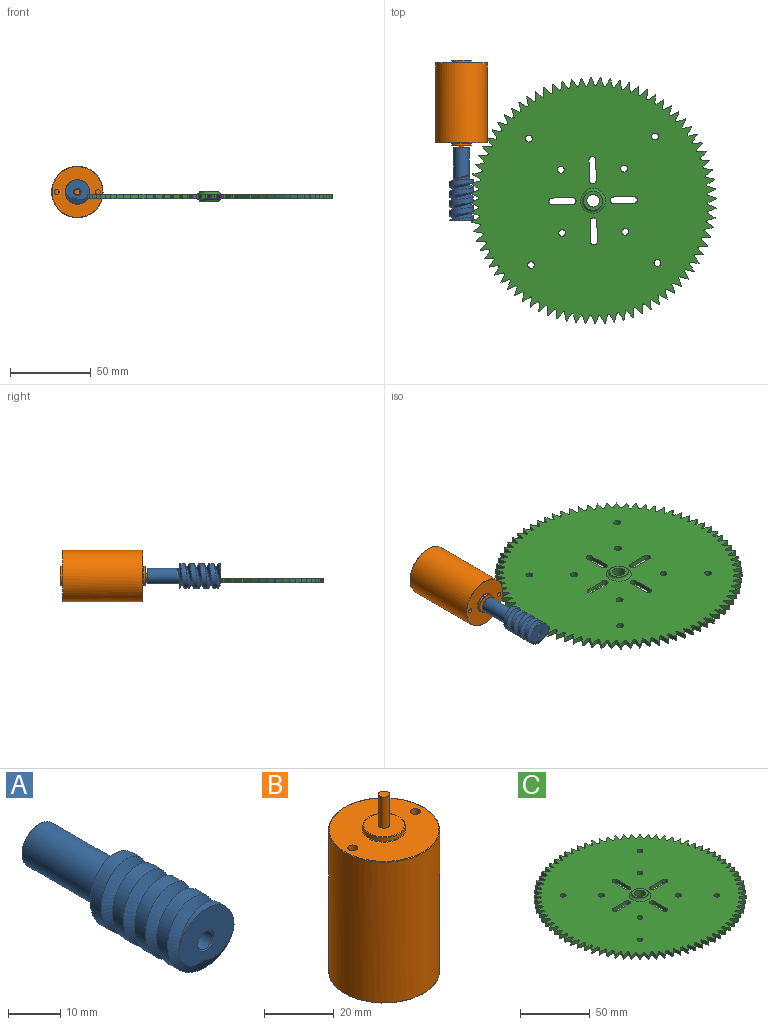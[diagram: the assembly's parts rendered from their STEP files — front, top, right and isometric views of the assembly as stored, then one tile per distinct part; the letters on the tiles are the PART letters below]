
ASSEMBLY  parts=3 mates=1
PART A: 12 faces, bbox 17.3x47.5x15 mm
  f0: cylinder r=4.76mm len=19.75mm, axis (0,-1,0), area 585.3mm2, adj f1,f5,f9,f10,f11
  f1: plane 15x12.23mm, normal (0,1,0), area 73.4mm2, adj f0,f2,f10,f11
  f2: cylinder r=7.5mm len=25.4mm, axis (0,1,0), area 597.9mm2, adj f1,f3,f10,f11
  f3: plane 14.95x12.4mm, normal (0,-1,0), area 127.1mm2, adj f2,f8,f10,f11
  f4: plane 9.03x9.03mm, normal (0,1,0), area 47.2mm2, adj f5,f7
  f5: cone r=4.51mm half-angle=45deg, axis (0,-1,0), area 10.3mm2, adj f0,f4
  f6: cylinder r=2.06mm len=44.9mm, axis (0,1,0), area 582.2mm2, adj f7,f8
  f7: cone r=2.06mm half-angle=45deg, axis (0,1,0), area 4.9mm2, adj f4,f6
  f8: cone r=2.31mm half-angle=45deg, axis (0,-1,0), area 4.9mm2, adj f3,f6
  f9: plane 0.47x0.44mm, normal (-0.5,0,0.87), area 0.1mm2, adj f0,f10,f11
  f10: bspline ~31.5x17.32mm, area 572.4mm2, adj f0,f1,f2,f3,f9,f11
  f11: bspline ~30.5x17.32mm, area 570.9mm2, adj f0,f1,f2,f3,f9,f10
PART B: 21 faces, bbox 34.4x34.4x63.6 mm
  f0: plane 11.63x11.63mm, normal (0,0,1), area 98.6mm2, adj f9,f16
  f1: cylinder r=1.55mm len=26.38mm, axis (0,0,1), area 256.9mm2, adj f2,f8
  f2: plane 11.63x11.63mm, normal (0,0,-1), area 98.7mm2, adj f1,f13
  f3: cylinder r=6.02mm len=12.03mm, axis (0,0,1), area 45.4mm2, adj f12,f13
  f4: plane 31.35x31.35mm, normal (0,0,-1), area 650.6mm2, adj f11,f12
  f5: cylinder r=15.88mm len=49.15mm, axis (0,0,1), area 4902.5mm2, adj f11,f14
  f6: plane 31.35x31.35mm, normal (0,0,1), area 638.2mm2, adj f14,f15,f17,f19
  f7: cylinder r=6.02mm len=12.03mm, axis (0,0,1), area 45.4mm2, adj f15,f16
  f8: plane 3.1x3.1mm, normal (0,0,-1), area 7.5mm2, adj f1
  f9: cylinder r=1.55mm len=10.83mm, axis (0,0,-1), area 105.8mm2, adj f0,f10
  f10: plane 3.11x3.11mm, normal (0,0,1), area 7.6mm2, adj f9
  f11: torus R=15.68mm, axis (0,0,-1), area 31.2mm2, adj f4,f5
  f12: torus R=6.21mm, axis (0,0,-1), area 12mm2, adj f3,f4
  f13: torus R=5.81mm, axis (0,0,-1), area 11.7mm2, adj f2,f3
  f14: torus R=15.68mm, axis (0,0,1), area 31.2mm2, adj f5,f6
  f15: torus R=6.21mm, axis (0,0,1), area 12mm2, adj f6,f7
  f16: torus R=5.81mm, axis (0,0,1), area 11.7mm2, adj f0,f7
  f17: cylinder r=1.4mm len=5mm, axis (0,0,1), area 44mm2, adj f6,f18
  f18: plane 2.8x2.8mm, normal (0,0,1), area 6.2mm2, adj f17
  f19: cylinder r=1.4mm len=5mm, axis (0,0,1), area 44mm2, adj f6,f20
  f20: plane 2.8x2.8mm, normal (0,0,1), area 6.2mm2, adj f19
PART C: 351 faces, bbox 152.4x152.4x9.2 mm
  f0: plane 152.4x152.4mm, normal (0,0,-1), area 16289.8mm2, adj f1,f2,f3,f4,f5,f6,f7,f8
  f1: cylinder r=76.2mm len=2.92mm, axis (0,0,-1), area 0.8mm2, adj f0,f81,f84,f320
  f2: cylinder r=76.2mm len=2.92mm, axis (0,0,-1), area 0.8mm2, adj f0,f81,f317,f321
  f3: cylinder r=76.2mm len=2.92mm, axis (0,0,-1), area 0.8mm2, adj f0,f81,f314,f318
  f4: cylinder r=76.2mm len=2.92mm, axis (0,0,-1), area 0.8mm2, adj f0,f81,f311,f315
  f5: cylinder r=76.2mm len=2.92mm, axis (0,0,-1), area 0.8mm2, adj f0,f81,f308,f312
  f6: cylinder r=76.2mm len=2.92mm, axis (0,0,-1), area 0.8mm2, adj f0,f81,f305,f309
  f7: cylinder r=76.2mm len=2.92mm, axis (0,0,-1), area 0.8mm2, adj f0,f81,f302,f306
  f8: cylinder r=76.2mm len=2.92mm, axis (0,0,-1), area 0.8mm2, adj f0,f81,f299,f303
  f9: cylinder r=76.2mm len=2.92mm, axis (0,0,-1), area 0.8mm2, adj f0,f81,f296,f300
  f10: cylinder r=76.2mm len=2.92mm, axis (0,0,-1), area 0.8mm2, adj f0,f81,f293,f297
  f11: cylinder r=76.2mm len=2.92mm, axis (0,0,-1), area 0.8mm2, adj f0,f81,f290,f294
  f12: cylinder r=76.2mm len=2.92mm, axis (0,0,-1), area 0.8mm2, adj f0,f81,f287,f291
  f13: cylinder r=76.2mm len=2.92mm, axis (0,0,-1), area 0.8mm2, adj f0,f81,f284,f288
  f14: cylinder r=76.2mm len=2.92mm, axis (0,0,-1), area 0.8mm2, adj f0,f81,f281,f285
  f15: cylinder r=76.2mm len=2.92mm, axis (0,0,-1), area 0.8mm2, adj f0,f81,f278,f282
  f16: cylinder r=76.2mm len=2.92mm, axis (0,0,-1), area 0.8mm2, adj f0,f81,f275,f279
  f17: cylinder r=76.2mm len=2.92mm, axis (0,0,-1), area 0.8mm2, adj f0,f81,f272,f276
  f18: cylinder r=76.2mm len=2.92mm, axis (0,0,-1), area 0.8mm2, adj f0,f81,f269,f273
  f19: cylinder r=76.2mm len=2.92mm, axis (0,0,-1), area 0.8mm2, adj f0,f81,f266,f270
  f20: cylinder r=76.2mm len=2.92mm, axis (0,0,-1), area 0.8mm2, adj f0,f81,f263,f267
  f21: cylinder r=76.2mm len=2.92mm, axis (0,0,-1), area 0.8mm2, adj f0,f81,f260,f264
  f22: cylinder r=76.2mm len=2.92mm, axis (0,0,-1), area 0.8mm2, adj f0,f81,f257,f261
  f23: cylinder r=76.2mm len=2.92mm, axis (0,0,-1), area 0.8mm2, adj f0,f81,f254,f258
  f24: cylinder r=76.2mm len=2.92mm, axis (0,0,-1), area 0.8mm2, adj f0,f81,f251,f255
  f25: cylinder r=76.2mm len=2.92mm, axis (0,0,-1), area 0.8mm2, adj f0,f81,f248,f252
  f26: cylinder r=76.2mm len=2.92mm, axis (0,0,-1), area 0.8mm2, adj f0,f81,f245,f249
  f27: cylinder r=76.2mm len=2.92mm, axis (0,0,-1), area 0.8mm2, adj f0,f81,f242,f246
  f28: cylinder r=76.2mm len=2.92mm, axis (0,0,-1), area 0.8mm2, adj f0,f81,f239,f243
  f29: cylinder r=76.2mm len=2.92mm, axis (0,0,-1), area 0.8mm2, adj f0,f81,f236,f240
  f30: cylinder r=76.2mm len=2.92mm, axis (0,0,-1), area 0.8mm2, adj f0,f81,f233,f237
  f31: cylinder r=76.2mm len=2.92mm, axis (0,0,-1), area 0.8mm2, adj f0,f81,f230,f234
  f32: cylinder r=76.2mm len=2.92mm, axis (0,0,-1), area 0.8mm2, adj f0,f81,f227,f231
  f33: cylinder r=76.2mm len=2.92mm, axis (0,0,-1), area 0.8mm2, adj f0,f81,f224,f228
  f34: cylinder r=76.2mm len=2.92mm, axis (0,0,-1), area 0.8mm2, adj f0,f81,f221,f225
  f35: cylinder r=76.2mm len=2.92mm, axis (0,0,-1), area 0.8mm2, adj f0,f81,f218,f222
  f36: cylinder r=76.2mm len=2.92mm, axis (0,0,-1), area 0.8mm2, adj f0,f81,f215,f219
  f37: cylinder r=76.2mm len=2.92mm, axis (0,0,-1), area 0.8mm2, adj f0,f81,f212,f216
  f38: cylinder r=76.2mm len=2.92mm, axis (0,0,-1), area 0.8mm2, adj f0,f81,f209,f213
  f39: cylinder r=76.2mm len=2.92mm, axis (0,0,-1), area 0.8mm2, adj f0,f81,f206,f210
  f40: cylinder r=76.2mm len=2.92mm, axis (0,0,-1), area 0.8mm2, adj f0,f81,f203,f207
  f41: cylinder r=76.2mm len=2.92mm, axis (0,0,-1), area 0.8mm2, adj f0,f81,f200,f204
  f42: cylinder r=76.2mm len=2.92mm, axis (0,0,-1), area 0.8mm2, adj f0,f81,f197,f201
  f43: cylinder r=76.2mm len=2.92mm, axis (0,0,-1), area 0.8mm2, adj f0,f81,f194,f198
  f44: cylinder r=76.2mm len=2.92mm, axis (0,0,-1), area 0.8mm2, adj f0,f81,f191,f195
  f45: cylinder r=76.2mm len=2.92mm, axis (0,0,-1), area 0.8mm2, adj f0,f81,f188,f192
  f46: cylinder r=76.2mm len=2.92mm, axis (0,0,-1), area 0.8mm2, adj f0,f81,f185,f189
  f47: cylinder r=76.2mm len=2.92mm, axis (0,0,-1), area 0.8mm2, adj f0,f81,f182,f186
  f48: cylinder r=76.2mm len=2.92mm, axis (0,0,-1), area 0.8mm2, adj f0,f81,f179,f183
  f49: cylinder r=76.2mm len=2.92mm, axis (0,0,-1), area 0.8mm2, adj f0,f81,f176,f180
  f50: cylinder r=76.2mm len=2.92mm, axis (0,0,-1), area 0.8mm2, adj f0,f81,f173,f177
  f51: cylinder r=76.2mm len=2.92mm, axis (0,0,-1), area 0.8mm2, adj f0,f81,f170,f174
  f52: cylinder r=76.2mm len=2.92mm, axis (0,0,-1), area 0.8mm2, adj f0,f81,f167,f171
  f53: cylinder r=76.2mm len=2.92mm, axis (0,0,-1), area 0.8mm2, adj f0,f81,f164,f168
  f54: cylinder r=76.2mm len=2.92mm, axis (0,0,-1), area 0.8mm2, adj f0,f81,f161,f165
  f55: cylinder r=76.2mm len=2.92mm, axis (0,0,-1), area 0.8mm2, adj f0,f81,f158,f162
  f56: cylinder r=76.2mm len=2.92mm, axis (0,0,-1), area 0.8mm2, adj f0,f81,f155,f159
  f57: cylinder r=76.2mm len=2.92mm, axis (0,0,-1), area 0.8mm2, adj f0,f81,f152,f156
  f58: cylinder r=76.2mm len=2.92mm, axis (0,0,-1), area 0.8mm2, adj f0,f81,f149,f153
  f59: cylinder r=76.2mm len=2.92mm, axis (0,0,-1), area 0.8mm2, adj f0,f81,f146,f150
  f60: cylinder r=76.2mm len=2.92mm, axis (0,0,-1), area 0.8mm2, adj f0,f81,f143,f147
  f61: cylinder r=76.2mm len=2.92mm, axis (0,0,-1), area 0.8mm2, adj f0,f81,f140,f144
  f62: cylinder r=76.2mm len=2.92mm, axis (0,0,-1), area 0.8mm2, adj f0,f81,f137,f141
  f63: cylinder r=76.2mm len=2.92mm, axis (0,0,-1), area 0.8mm2, adj f0,f81,f134,f138
  f64: cylinder r=76.2mm len=2.92mm, axis (0,0,-1), area 0.8mm2, adj f0,f81,f131,f135
  f65: cylinder r=76.2mm len=2.92mm, axis (0,0,-1), area 0.8mm2, adj f0,f81,f128,f132
  f66: cylinder r=76.2mm len=2.92mm, axis (0,0,-1), area 0.8mm2, adj f0,f81,f125,f129
  f67: cylinder r=76.2mm len=2.92mm, axis (0,0,-1), area 0.8mm2, adj f0,f81,f122,f126
  f68: cylinder r=76.2mm len=2.92mm, axis (0,0,-1), area 0.8mm2, adj f0,f81,f119,f123
  f69: cylinder r=76.2mm len=2.92mm, axis (0,0,-1), area 0.8mm2, adj f0,f81,f116,f120
  f70: cylinder r=76.2mm len=2.92mm, axis (0,0,-1), area 0.8mm2, adj f0,f81,f113,f117
  f71: cylinder r=76.2mm len=2.92mm, axis (0,0,-1), area 0.8mm2, adj f0,f81,f110,f114
  f72: cylinder r=76.2mm len=2.92mm, axis (0,0,-1), area 0.8mm2, adj f0,f81,f107,f111
  f73: cylinder r=76.2mm len=2.92mm, axis (0,0,-1), area 0.8mm2, adj f0,f81,f104,f108
  f74: cylinder r=76.2mm len=2.92mm, axis (0,0,-1), area 0.8mm2, adj f0,f81,f101,f105
  f75: cylinder r=76.2mm len=2.92mm, axis (0,0,-1), area 0.8mm2, adj f0,f81,f98,f102
  f76: cylinder r=76.2mm len=2.92mm, axis (0,0,-1), area 0.8mm2, adj f0,f81,f95,f99
  f77: cylinder r=76.2mm len=2.92mm, axis (0,0,-1), area 0.8mm2, adj f0,f81,f92,f96
  f78: cylinder r=76.2mm len=2.92mm, axis (0,0,-1), area 0.8mm2, adj f0,f81,f89,f93
  f79: cylinder r=76.2mm len=2.92mm, axis (0,0,-1), area 0.8mm2, adj f0,f81,f86,f90
  f80: cylinder r=76.2mm len=2.92mm, axis (0,0,-1), area 0.8mm2, adj f0,f81,f83,f87
  f81: plane 152.4x152.4mm, normal (0,0,1), area 16289.8mm2, adj f1,f2,f3,f4,f5,f6,f7,f8
  f82: cylinder r=71.06mm len=2.92mm, axis (0,0,-1), area 2.9mm2, adj f0,f81,f83,f84
  f83: plane 5x2.92mm, normal (0.89,-0.45,0), area 16.4mm2, adj f0,f80,f81,f82
  f84: plane 5.18x2.92mm, normal (-0.92,-0.38,0), area 16.4mm2, adj f0,f1,f81,f82
  f85: cylinder r=71.06mm len=2.92mm, axis (0,0,-1), area 2.9mm2, adj f0,f81,f86,f87
  f86: plane 4.78x2.93mm, normal (0.85,-0.52,0), area 16.4mm2, adj f0,f79,f81,f85
  f87: plane 5.33x2.92mm, normal (-0.95,-0.31,0), area 16.4mm2, adj f0,f80,f81,f85
  f88: cylinder r=71.06mm len=2.92mm, axis (0,0,-1), area 2.9mm2, adj f0,f81,f89,f90
  f89: plane 4.54x3.3mm, normal (0.81,-0.59,0), area 16.4mm2, adj f0,f78,f81,f88
  f90: plane 5.45x2.92mm, normal (-0.97,-0.23,0), area 16.4mm2, adj f0,f79,f81,f88
  f91: cylinder r=71.06mm len=2.92mm, axis (0,0,-1), area 2.9mm2, adj f0,f81,f92,f93
  f92: plane 4.26x3.64mm, normal (0.76,-0.65,0), area 16.4mm2, adj f0,f77,f81,f91
  f93: plane 5.54x2.92mm, normal (-0.99,-0.16,0), area 16.4mm2, adj f0,f78,f81,f91
  f94: cylinder r=71.06mm len=2.92mm, axis (0,0,-1), area 2.9mm2, adj f0,f81,f95,f96
  f95: plane 3.97x3.97mm, normal (0.71,-0.71,0), area 16.4mm2, adj f0,f76,f81,f94
  f96: plane 5.59x2.92mm, normal (-1,-0.08,0), area 16.4mm2, adj f0,f77,f81,f94
  f97: cylinder r=71.06mm len=2.92mm, axis (0,0,-1), area 2.9mm2, adj f0,f81,f98,f99
  f98: plane 4.27x3.64mm, normal (0.65,-0.76,0), area 16.4mm2, adj f0,f75,f81,f97
  f99: plane 5.61x2.92mm, normal (-1,0,0), area 16.4mm2, adj f0,f76,f81,f97
  f100: cylinder r=71.06mm len=2.92mm, axis (0,0,-1), area 2.9mm2, adj f0,f81,f101,f102
  f101: plane 4.54x3.3mm, normal (0.59,-0.81,0), area 16.4mm2, adj f0,f74,f81,f100
  f102: plane 5.59x2.92mm, normal (-1,0.08,0), area 16.4mm2, adj f0,f75,f81,f100
  f103: cylinder r=71.06mm len=2.92mm, axis (0,0,-1), area 2.9mm2, adj f0,f81,f104,f105
  f104: plane 4.78x2.93mm, normal (0.52,-0.85,0), area 16.4mm2, adj f0,f73,f81,f103
  f105: plane 5.54x2.92mm, normal (-0.99,0.16,0), area 16.4mm2, adj f0,f74,f81,f103
  f106: cylinder r=71.06mm len=2.92mm, axis (0,0,-1), area 2.9mm2, adj f0,f81,f107,f108
  f107: plane 5x2.92mm, normal (0.45,-0.89,0), area 16.4mm2, adj f0,f72,f81,f106
  f108: plane 5.45x2.92mm, normal (-0.97,0.23,0), area 16.4mm2, adj f0,f73,f81,f106
  f109: cylinder r=71.06mm len=2.92mm, axis (0,0,-1), area 2.9mm2, adj f0,f81,f110,f111
  f110: plane 5.18x2.92mm, normal (0.38,-0.92,0), area 16.4mm2, adj f0,f71,f81,f109
  f111: plane 5.33x2.92mm, normal (-0.95,0.31,0), area 16.4mm2, adj f0,f72,f81,f109
  f112: cylinder r=71.06mm len=2.92mm, axis (0,0,-1), area 2.9mm2, adj f0,f81,f113,f114
  f113: plane 5.34x2.92mm, normal (0.31,-0.95,0), area 16.4mm2, adj f0,f70,f81,f112
  f114: plane 5.18x2.92mm, normal (-0.92,0.38,0), area 16.4mm2, adj f0,f71,f81,f112
  f115: cylinder r=71.06mm len=2.92mm, axis (0,0,-1), area 2.9mm2, adj f0,f81,f116,f117
  f116: plane 5.45x2.92mm, normal (0.23,-0.97,0), area 16.4mm2, adj f0,f69,f81,f115
  f117: plane 5x2.92mm, normal (-0.89,0.45,0), area 16.4mm2, adj f0,f70,f81,f115
  f118: cylinder r=71.06mm len=2.92mm, axis (0,0,-1), area 2.9mm2, adj f0,f81,f119,f120
  f119: plane 5.54x2.92mm, normal (0.16,-0.99,0), area 16.4mm2, adj f0,f68,f81,f118
  f120: plane 4.78x2.93mm, normal (-0.85,0.52,0), area 16.4mm2, adj f0,f69,f81,f118
  f121: cylinder r=71.06mm len=2.92mm, axis (0,0,-1), area 2.9mm2, adj f0,f81,f122,f123
  f122: plane 5.59x2.92mm, normal (0.08,-1,0), area 16.4mm2, adj f0,f67,f81,f121
  f123: plane 4.54x3.3mm, normal (-0.81,0.59,0), area 16.4mm2, adj f0,f68,f81,f121
  f124: cylinder r=71.06mm len=2.92mm, axis (0,0,-1), area 2.9mm2, adj f0,f81,f125,f126
  f125: plane 5.61x2.92mm, normal (0,-1,0), area 16.4mm2, adj f0,f66,f81,f124
  f126: plane 4.27x3.64mm, normal (-0.76,0.65,0), area 16.4mm2, adj f0,f67,f81,f124
  f127: cylinder r=71.06mm len=2.92mm, axis (0,0,-1), area 2.9mm2, adj f0,f81,f128,f129
  f128: plane 5.59x2.92mm, normal (-0.08,-1,0), area 16.4mm2, adj f0,f65,f81,f127
  f129: plane 3.97x3.97mm, normal (-0.71,0.71,0), area 16.4mm2, adj f0,f66,f81,f127
  f130: cylinder r=71.06mm len=2.92mm, axis (0,0,-1), area 2.9mm2, adj f0,f81,f131,f132
  f131: plane 5.54x2.92mm, normal (-0.16,-0.99,0), area 16.4mm2, adj f0,f64,f81,f130
  f132: plane 4.27x3.64mm, normal (-0.65,0.76,0), area 16.4mm2, adj f0,f65,f81,f130
  f133: cylinder r=71.06mm len=2.92mm, axis (0,0,-1), area 2.9mm2, adj f0,f81,f134,f135
  f134: plane 5.45x2.92mm, normal (-0.23,-0.97,0), area 16.4mm2, adj f0,f63,f81,f133
  f135: plane 4.54x3.3mm, normal (-0.59,0.81,0), area 16.4mm2, adj f0,f64,f81,f133
  f136: cylinder r=71.06mm len=2.92mm, axis (0,0,-1), area 2.9mm2, adj f0,f81,f137,f138
  f137: plane 5.33x2.92mm, normal (-0.31,-0.95,0), area 16.4mm2, adj f0,f62,f81,f136
  f138: plane 4.78x2.93mm, normal (-0.52,0.85,0), area 16.4mm2, adj f0,f63,f81,f136
  f139: cylinder r=71.06mm len=2.92mm, axis (0,0,-1), area 2.9mm2, adj f0,f81,f140,f141
  f140: plane 5.18x2.92mm, normal (-0.38,-0.92,0), area 16.4mm2, adj f0,f61,f81,f139
  f141: plane 5x2.92mm, normal (-0.45,0.89,0), area 16.4mm2, adj f0,f62,f81,f139
  f142: cylinder r=71.06mm len=2.92mm, axis (0,0,-1), area 2.9mm2, adj f0,f81,f143,f144
  f143: plane 5x2.92mm, normal (-0.45,-0.89,0), area 16.4mm2, adj f0,f60,f81,f142
  f144: plane 5.18x2.92mm, normal (-0.38,0.92,0), area 16.4mm2, adj f0,f61,f81,f142
  f145: cylinder r=71.06mm len=2.92mm, axis (0,0,-1), area 2.9mm2, adj f0,f81,f146,f147
  f146: plane 4.78x2.93mm, normal (-0.52,-0.85,0), area 16.4mm2, adj f0,f59,f81,f145
  f147: plane 5.33x2.92mm, normal (-0.31,0.95,0), area 16.4mm2, adj f0,f60,f81,f145
  f148: cylinder r=71.06mm len=2.92mm, axis (0,0,-1), area 2.9mm2, adj f0,f81,f149,f150
  f149: plane 4.54x3.3mm, normal (-0.59,-0.81,0), area 16.4mm2, adj f0,f58,f81,f148
  f150: plane 5.45x2.92mm, normal (-0.23,0.97,0), area 16.4mm2, adj f0,f59,f81,f148
  f151: cylinder r=71.06mm len=2.92mm, axis (0,0,-1), area 2.9mm2, adj f0,f81,f152,f153
  f152: plane 4.26x3.64mm, normal (-0.65,-0.76,0), area 16.4mm2, adj f0,f57,f81,f151
  f153: plane 5.54x2.92mm, normal (-0.16,0.99,0), area 16.4mm2, adj f0,f58,f81,f151
  f154: cylinder r=71.06mm len=2.92mm, axis (0,0,-1), area 2.9mm2, adj f0,f81,f155,f156
  f155: plane 3.97x3.97mm, normal (-0.71,-0.71,0), area 16.4mm2, adj f0,f56,f81,f154
  f156: plane 5.59x2.92mm, normal (-0.08,1,0), area 16.4mm2, adj f0,f57,f81,f154
  f157: cylinder r=71.06mm len=2.92mm, axis (0,0,-1), area 2.9mm2, adj f0,f81,f158,f159
  f158: plane 4.27x3.64mm, normal (-0.76,-0.65,0), area 16.4mm2, adj f0,f55,f81,f157
  f159: plane 5.61x2.92mm, normal (0,1,0), area 16.4mm2, adj f0,f56,f81,f157
  f160: cylinder r=71.06mm len=2.92mm, axis (0,0,-1), area 2.9mm2, adj f0,f81,f161,f162
  f161: plane 4.54x3.3mm, normal (-0.81,-0.59,0), area 16.4mm2, adj f0,f54,f81,f160
  f162: plane 5.59x2.92mm, normal (0.08,1,0), area 16.4mm2, adj f0,f55,f81,f160
  f163: cylinder r=71.06mm len=2.92mm, axis (0,0,-1), area 2.9mm2, adj f0,f81,f164,f165
  f164: plane 4.78x2.93mm, normal (-0.85,-0.52,0), area 16.4mm2, adj f0,f53,f81,f163
  f165: plane 5.54x2.92mm, normal (0.16,0.99,0), area 16.4mm2, adj f0,f54,f81,f163
  f166: cylinder r=71.06mm len=2.92mm, axis (0,0,-1), area 2.9mm2, adj f0,f81,f167,f168
  f167: plane 5x2.92mm, normal (-0.89,-0.45,0), area 16.4mm2, adj f0,f52,f81,f166
  f168: plane 5.45x2.92mm, normal (0.23,0.97,0), area 16.4mm2, adj f0,f53,f81,f166
  f169: cylinder r=71.06mm len=2.92mm, axis (0,0,-1), area 2.9mm2, adj f0,f81,f170,f171
  f170: plane 5.18x2.92mm, normal (-0.92,-0.38,0), area 16.4mm2, adj f0,f51,f81,f169
  f171: plane 5.33x2.92mm, normal (0.31,0.95,0), area 16.4mm2, adj f0,f52,f81,f169
  f172: cylinder r=71.06mm len=2.92mm, axis (0,0,-1), area 2.9mm2, adj f0,f81,f173,f174
  f173: plane 5.34x2.92mm, normal (-0.95,-0.31,0), area 16.4mm2, adj f0,f50,f81,f172
  f174: plane 5.18x2.92mm, normal (0.38,0.92,0), area 16.4mm2, adj f0,f51,f81,f172
  f175: cylinder r=71.06mm len=2.92mm, axis (0,0,-1), area 2.9mm2, adj f0,f81,f176,f177
  f176: plane 5.45x2.92mm, normal (-0.97,-0.23,0), area 16.4mm2, adj f0,f49,f81,f175
  f177: plane 5x2.92mm, normal (0.45,0.89,0), area 16.4mm2, adj f0,f50,f81,f175
  f178: cylinder r=71.06mm len=2.92mm, axis (0,0,-1), area 2.9mm2, adj f0,f81,f179,f180
  f179: plane 5.54x2.92mm, normal (-0.99,-0.16,0), area 16.4mm2, adj f0,f48,f81,f178
  f180: plane 4.78x2.93mm, normal (0.52,0.85,0), area 16.4mm2, adj f0,f49,f81,f178
  f181: cylinder r=71.06mm len=2.92mm, axis (0,0,-1), area 2.9mm2, adj f0,f81,f182,f183
  f182: plane 5.59x2.92mm, normal (-1,-0.08,0), area 16.4mm2, adj f0,f47,f81,f181
  f183: plane 4.54x3.3mm, normal (0.59,0.81,0), area 16.4mm2, adj f0,f48,f81,f181
  f184: cylinder r=71.06mm len=2.92mm, axis (0,0,-1), area 2.9mm2, adj f0,f81,f185,f186
  f185: plane 5.61x2.92mm, normal (-1,0,0), area 16.4mm2, adj f0,f46,f81,f184
  f186: plane 4.27x3.64mm, normal (0.65,0.76,0), area 16.4mm2, adj f0,f47,f81,f184
  f187: cylinder r=71.06mm len=2.92mm, axis (0,0,-1), area 2.9mm2, adj f0,f81,f188,f189
  f188: plane 5.59x2.92mm, normal (-1,0.08,0), area 16.4mm2, adj f0,f45,f81,f187
  f189: plane 3.97x3.97mm, normal (0.71,0.71,0), area 16.4mm2, adj f0,f46,f81,f187
  f190: cylinder r=71.06mm len=2.92mm, axis (0,0,-1), area 2.9mm2, adj f0,f81,f191,f192
  f191: plane 5.54x2.92mm, normal (-0.99,0.16,0), area 16.4mm2, adj f0,f44,f81,f190
  f192: plane 4.27x3.64mm, normal (0.76,0.65,0), area 16.4mm2, adj f0,f45,f81,f190
  f193: cylinder r=71.06mm len=2.92mm, axis (0,0,-1), area 2.9mm2, adj f0,f81,f194,f195
  f194: plane 5.45x2.92mm, normal (-0.97,0.23,0), area 16.4mm2, adj f0,f43,f81,f193
  f195: plane 4.54x3.3mm, normal (0.81,0.59,0), area 16.4mm2, adj f0,f44,f81,f193
  f196: cylinder r=71.06mm len=2.92mm, axis (0,0,-1), area 2.9mm2, adj f0,f81,f197,f198
  f197: plane 5.33x2.92mm, normal (-0.95,0.31,0), area 16.4mm2, adj f0,f42,f81,f196
  f198: plane 4.78x2.93mm, normal (0.85,0.52,0), area 16.4mm2, adj f0,f43,f81,f196
  f199: cylinder r=71.06mm len=2.92mm, axis (0,0,-1), area 2.9mm2, adj f0,f81,f200,f201
  f200: plane 5.18x2.92mm, normal (-0.92,0.38,0), area 16.4mm2, adj f0,f41,f81,f199
  f201: plane 5x2.92mm, normal (0.89,0.45,0), area 16.4mm2, adj f0,f42,f81,f199
  f202: cylinder r=71.06mm len=2.92mm, axis (0,0,-1), area 2.9mm2, adj f0,f81,f203,f204
  f203: plane 5x2.92mm, normal (-0.89,0.45,0), area 16.4mm2, adj f0,f40,f81,f202
  f204: plane 5.18x2.92mm, normal (0.92,0.38,0), area 16.4mm2, adj f0,f41,f81,f202
  f205: cylinder r=71.06mm len=2.92mm, axis (0,0,-1), area 2.9mm2, adj f0,f81,f206,f207
  f206: plane 4.78x2.93mm, normal (-0.85,0.52,0), area 16.4mm2, adj f0,f39,f81,f205
  f207: plane 5.33x2.92mm, normal (0.95,0.31,0), area 16.4mm2, adj f0,f40,f81,f205
  f208: cylinder r=71.06mm len=2.92mm, axis (0,0,-1), area 2.9mm2, adj f0,f81,f209,f210
  f209: plane 4.54x3.3mm, normal (-0.81,0.59,0), area 16.4mm2, adj f0,f38,f81,f208
  f210: plane 5.45x2.92mm, normal (0.97,0.23,0), area 16.4mm2, adj f0,f39,f81,f208
  f211: cylinder r=71.06mm len=2.92mm, axis (0,0,-1), area 2.9mm2, adj f0,f81,f212,f213
  f212: plane 4.26x3.64mm, normal (-0.76,0.65,0), area 16.4mm2, adj f0,f37,f81,f211
  f213: plane 5.54x2.92mm, normal (0.99,0.16,0), area 16.4mm2, adj f0,f38,f81,f211
  f214: cylinder r=71.06mm len=2.92mm, axis (0,0,-1), area 2.9mm2, adj f0,f81,f215,f216
  f215: plane 3.97x3.97mm, normal (-0.71,0.71,0), area 16.4mm2, adj f0,f36,f81,f214
  f216: plane 5.59x2.92mm, normal (1,0.08,0), area 16.4mm2, adj f0,f37,f81,f214
  f217: cylinder r=71.06mm len=2.92mm, axis (0,0,-1), area 2.9mm2, adj f0,f81,f218,f219
  f218: plane 4.27x3.64mm, normal (-0.65,0.76,0), area 16.4mm2, adj f0,f35,f81,f217
  f219: plane 5.61x2.92mm, normal (1,0,0), area 16.4mm2, adj f0,f36,f81,f217
  f220: cylinder r=71.06mm len=2.92mm, axis (0,0,-1), area 2.9mm2, adj f0,f81,f221,f222
  f221: plane 4.54x3.3mm, normal (-0.59,0.81,0), area 16.4mm2, adj f0,f34,f81,f220
  f222: plane 5.59x2.92mm, normal (1,-0.08,0), area 16.4mm2, adj f0,f35,f81,f220
  f223: cylinder r=71.06mm len=2.92mm, axis (0,0,-1), area 2.9mm2, adj f0,f81,f224,f225
  f224: plane 4.78x2.93mm, normal (-0.52,0.85,0), area 16.4mm2, adj f0,f33,f81,f223
  f225: plane 5.54x2.92mm, normal (0.99,-0.16,0), area 16.4mm2, adj f0,f34,f81,f223
  f226: cylinder r=71.06mm len=2.92mm, axis (0,0,-1), area 2.9mm2, adj f0,f81,f227,f228
  f227: plane 5x2.92mm, normal (-0.45,0.89,0), area 16.4mm2, adj f0,f32,f81,f226
  f228: plane 5.45x2.92mm, normal (0.97,-0.23,0), area 16.4mm2, adj f0,f33,f81,f226
  f229: cylinder r=71.06mm len=2.92mm, axis (0,0,-1), area 2.9mm2, adj f0,f81,f230,f231
  f230: plane 5.18x2.92mm, normal (-0.38,0.92,0), area 16.4mm2, adj f0,f31,f81,f229
  f231: plane 5.33x2.92mm, normal (0.95,-0.31,0), area 16.4mm2, adj f0,f32,f81,f229
  f232: cylinder r=71.06mm len=2.92mm, axis (0,0,-1), area 2.9mm2, adj f0,f81,f233,f234
  f233: plane 5.34x2.92mm, normal (-0.31,0.95,0), area 16.4mm2, adj f0,f30,f81,f232
  f234: plane 5.18x2.92mm, normal (0.92,-0.38,0), area 16.4mm2, adj f0,f31,f81,f232
  f235: cylinder r=71.06mm len=2.92mm, axis (0,0,-1), area 2.9mm2, adj f0,f81,f236,f237
  f236: plane 5.45x2.92mm, normal (-0.23,0.97,0), area 16.4mm2, adj f0,f29,f81,f235
  f237: plane 5x2.92mm, normal (0.89,-0.45,0), area 16.4mm2, adj f0,f30,f81,f235
  f238: cylinder r=71.06mm len=2.92mm, axis (0,0,-1), area 2.9mm2, adj f0,f81,f239,f240
  f239: plane 5.54x2.92mm, normal (-0.16,0.99,0), area 16.4mm2, adj f0,f28,f81,f238
  f240: plane 4.78x2.93mm, normal (0.85,-0.52,0), area 16.4mm2, adj f0,f29,f81,f238
  f241: cylinder r=71.06mm len=2.92mm, axis (0,0,-1), area 2.9mm2, adj f0,f81,f242,f243
  f242: plane 5.59x2.92mm, normal (-0.08,1,0), area 16.4mm2, adj f0,f27,f81,f241
  f243: plane 4.54x3.3mm, normal (0.81,-0.59,0), area 16.4mm2, adj f0,f28,f81,f241
  f244: cylinder r=71.06mm len=2.92mm, axis (0,0,-1), area 2.9mm2, adj f0,f81,f245,f246
  f245: plane 5.61x2.92mm, normal (0,1,0), area 16.4mm2, adj f0,f26,f81,f244
  f246: plane 4.27x3.64mm, normal (0.76,-0.65,0), area 16.4mm2, adj f0,f27,f81,f244
  f247: cylinder r=71.06mm len=2.92mm, axis (0,0,-1), area 2.9mm2, adj f0,f81,f248,f249
  f248: plane 5.59x2.92mm, normal (0.08,1,0), area 16.4mm2, adj f0,f25,f81,f247
  f249: plane 3.97x3.97mm, normal (0.71,-0.71,0), area 16.4mm2, adj f0,f26,f81,f247
  f250: cylinder r=71.06mm len=2.92mm, axis (0,0,-1), area 2.9mm2, adj f0,f81,f251,f252
  f251: plane 5.54x2.92mm, normal (0.16,0.99,0), area 16.4mm2, adj f0,f24,f81,f250
  f252: plane 4.27x3.64mm, normal (0.65,-0.76,0), area 16.4mm2, adj f0,f25,f81,f250
  f253: cylinder r=71.06mm len=2.92mm, axis (0,0,-1), area 2.9mm2, adj f0,f81,f254,f255
  f254: plane 5.45x2.92mm, normal (0.23,0.97,0), area 16.4mm2, adj f0,f23,f81,f253
  f255: plane 4.54x3.3mm, normal (0.59,-0.81,0), area 16.4mm2, adj f0,f24,f81,f253
  f256: cylinder r=71.06mm len=2.92mm, axis (0,0,-1), area 2.9mm2, adj f0,f81,f257,f258
  f257: plane 5.33x2.92mm, normal (0.31,0.95,0), area 16.4mm2, adj f0,f22,f81,f256
  f258: plane 4.78x2.93mm, normal (0.52,-0.85,0), area 16.4mm2, adj f0,f23,f81,f256
  f259: cylinder r=71.06mm len=2.92mm, axis (0,0,-1), area 2.9mm2, adj f0,f81,f260,f261
  f260: plane 5.18x2.92mm, normal (0.38,0.92,0), area 16.4mm2, adj f0,f21,f81,f259
  f261: plane 5x2.92mm, normal (0.45,-0.89,0), area 16.4mm2, adj f0,f22,f81,f259
  f262: cylinder r=71.06mm len=2.92mm, axis (0,0,-1), area 2.9mm2, adj f0,f81,f263,f264
  f263: plane 5x2.92mm, normal (0.45,0.89,0), area 16.4mm2, adj f0,f20,f81,f262
  f264: plane 5.18x2.92mm, normal (0.38,-0.92,0), area 16.4mm2, adj f0,f21,f81,f262
  f265: cylinder r=71.06mm len=2.92mm, axis (0,0,-1), area 2.9mm2, adj f0,f81,f266,f267
  f266: plane 4.78x2.93mm, normal (0.52,0.85,0), area 16.4mm2, adj f0,f19,f81,f265
  f267: plane 5.33x2.92mm, normal (0.31,-0.95,0), area 16.4mm2, adj f0,f20,f81,f265
  f268: cylinder r=71.06mm len=2.92mm, axis (0,0,-1), area 2.9mm2, adj f0,f81,f269,f270
  f269: plane 4.54x3.3mm, normal (0.59,0.81,0), area 16.4mm2, adj f0,f18,f81,f268
  f270: plane 5.45x2.92mm, normal (0.23,-0.97,0), area 16.4mm2, adj f0,f19,f81,f268
  f271: cylinder r=71.06mm len=2.92mm, axis (0,0,-1), area 2.9mm2, adj f0,f81,f272,f273
  f272: plane 4.26x3.64mm, normal (0.65,0.76,0), area 16.4mm2, adj f0,f17,f81,f271
  f273: plane 5.54x2.92mm, normal (0.16,-0.99,0), area 16.4mm2, adj f0,f18,f81,f271
  f274: cylinder r=71.06mm len=2.92mm, axis (0,0,-1), area 2.9mm2, adj f0,f81,f275,f276
  f275: plane 3.97x3.97mm, normal (0.71,0.71,0), area 16.4mm2, adj f0,f16,f81,f274
  f276: plane 5.59x2.92mm, normal (0.08,-1,0), area 16.4mm2, adj f0,f17,f81,f274
  f277: cylinder r=71.06mm len=2.92mm, axis (0,0,-1), area 2.9mm2, adj f0,f81,f278,f279
  f278: plane 4.27x3.64mm, normal (0.76,0.65,0), area 16.4mm2, adj f0,f15,f81,f277
  f279: plane 5.61x2.92mm, normal (0,-1,0), area 16.4mm2, adj f0,f16,f81,f277
  f280: cylinder r=71.06mm len=2.92mm, axis (0,0,-1), area 2.9mm2, adj f0,f81,f281,f282
  f281: plane 4.54x3.3mm, normal (0.81,0.59,0), area 16.4mm2, adj f0,f14,f81,f280
  f282: plane 5.59x2.92mm, normal (-0.08,-1,0), area 16.4mm2, adj f0,f15,f81,f280
  f283: cylinder r=71.06mm len=2.92mm, axis (0,0,-1), area 2.9mm2, adj f0,f81,f284,f285
  f284: plane 4.78x2.93mm, normal (0.85,0.52,0), area 16.4mm2, adj f0,f13,f81,f283
  f285: plane 5.54x2.92mm, normal (-0.16,-0.99,0), area 16.4mm2, adj f0,f14,f81,f283
  f286: cylinder r=71.06mm len=2.92mm, axis (0,0,-1), area 2.9mm2, adj f0,f81,f287,f288
  f287: plane 5x2.92mm, normal (0.89,0.45,0), area 16.4mm2, adj f0,f12,f81,f286
  f288: plane 5.45x2.92mm, normal (-0.23,-0.97,0), area 16.4mm2, adj f0,f13,f81,f286
  f289: cylinder r=71.06mm len=2.92mm, axis (0,0,-1), area 2.9mm2, adj f0,f81,f290,f291
  f290: plane 5.18x2.92mm, normal (0.92,0.38,0), area 16.4mm2, adj f0,f11,f81,f289
  f291: plane 5.33x2.92mm, normal (-0.31,-0.95,0), area 16.4mm2, adj f0,f12,f81,f289
  f292: cylinder r=71.06mm len=2.92mm, axis (0,0,-1), area 2.9mm2, adj f0,f81,f293,f294
  f293: plane 5.34x2.92mm, normal (0.95,0.31,0), area 16.4mm2, adj f0,f10,f81,f292
  f294: plane 5.18x2.92mm, normal (-0.38,-0.92,0), area 16.4mm2, adj f0,f11,f81,f292
  f295: cylinder r=71.06mm len=2.92mm, axis (0,0,-1), area 2.9mm2, adj f0,f81,f296,f297
  f296: plane 5.45x2.92mm, normal (0.97,0.23,0), area 16.4mm2, adj f0,f9,f81,f295
  f297: plane 5x2.92mm, normal (-0.45,-0.89,0), area 16.4mm2, adj f0,f10,f81,f295
  f298: cylinder r=71.06mm len=2.92mm, axis (0,0,-1), area 2.9mm2, adj f0,f81,f299,f300
  f299: plane 5.54x2.92mm, normal (0.99,0.16,0), area 16.4mm2, adj f0,f8,f81,f298
  f300: plane 4.78x2.93mm, normal (-0.52,-0.85,0), area 16.4mm2, adj f0,f9,f81,f298
  f301: cylinder r=71.06mm len=2.92mm, axis (0,0,-1), area 2.9mm2, adj f0,f81,f302,f303
  f302: plane 5.59x2.92mm, normal (1,0.08,0), area 16.4mm2, adj f0,f7,f81,f301
  f303: plane 4.54x3.3mm, normal (-0.59,-0.81,0), area 16.4mm2, adj f0,f8,f81,f301
  f304: cylinder r=71.06mm len=2.92mm, axis (0,0,-1), area 2.9mm2, adj f0,f81,f305,f306
  f305: plane 5.61x2.92mm, normal (1,0,0), area 16.4mm2, adj f0,f6,f81,f304
  f306: plane 4.27x3.64mm, normal (-0.65,-0.76,0), area 16.4mm2, adj f0,f7,f81,f304
  f307: cylinder r=71.06mm len=2.92mm, axis (0,0,-1), area 2.9mm2, adj f0,f81,f308,f309
  f308: plane 5.59x2.92mm, normal (1,-0.08,0), area 16.4mm2, adj f0,f5,f81,f307
  f309: plane 3.97x3.97mm, normal (-0.71,-0.71,0), area 16.4mm2, adj f0,f6,f81,f307
  f310: cylinder r=71.06mm len=2.92mm, axis (0,0,-1), area 2.9mm2, adj f0,f81,f311,f312
  f311: plane 5.54x2.92mm, normal (0.99,-0.16,0), area 16.4mm2, adj f0,f4,f81,f310
  f312: plane 4.27x3.64mm, normal (-0.76,-0.65,0), area 16.4mm2, adj f0,f5,f81,f310
  f313: cylinder r=71.06mm len=2.92mm, axis (0,0,-1), area 2.9mm2, adj f0,f81,f314,f315
  f314: plane 5.45x2.92mm, normal (0.97,-0.23,0), area 16.4mm2, adj f0,f3,f81,f313
  f315: plane 4.54x3.3mm, normal (-0.81,-0.59,0), area 16.4mm2, adj f0,f4,f81,f313
  f316: cylinder r=71.06mm len=2.92mm, axis (0,0,-1), area 2.9mm2, adj f0,f81,f317,f318
  f317: plane 5.33x2.92mm, normal (0.95,-0.31,0), area 16.4mm2, adj f0,f2,f81,f316
  f318: plane 4.78x2.93mm, normal (-0.85,-0.52,0), area 16.4mm2, adj f0,f3,f81,f316
  f319: cylinder r=71.06mm len=2.92mm, axis (0,0,-1), area 2.9mm2, adj f0,f81,f320,f321
  f320: plane 5.18x2.92mm, normal (0.92,-0.38,0), area 16.4mm2, adj f0,f1,f81,f319
  f321: plane 5x2.92mm, normal (-0.89,-0.45,0), area 16.4mm2, adj f0,f2,f81,f319
  f322: plane 11.74x11.74mm, normal (0,0,-1), area 60.1mm2, adj f323,f326
  f323: torus R=7.7mm, axis (0,0,1), area 117.9mm2, adj f0,f322
  f324: plane 11.74x11.74mm, normal (0,0,1), area 60.1mm2, adj f325,f326
  f325: torus R=7.7mm, axis (0,0,1), area 117.9mm2, adj f81,f324
  f326: cylinder r=3.91mm len=7.82mm, axis (0,0,-1), area 161.7mm2, adj f322,f324
  f327: cylinder r=2.12mm len=4.24mm, axis (0,0,1), area 19.5mm2, adj f0,f81,f328,f330
  f328: plane 12.6x2.92mm, normal (0,1,0), area 36.8mm2, adj f0,f81,f327,f329
  f329: cylinder r=2.12mm len=4.24mm, axis (0,0,1), area 19.5mm2, adj f0,f81,f328,f330
  f330: plane 12.6x2.92mm, normal (0,-1,0), area 36.8mm2, adj f0,f81,f327,f329
  f331: cylinder r=2.12mm len=4.24mm, axis (0,0,1), area 19.5mm2, adj f0,f81,f332,f334
  f332: plane 12.6x2.92mm, normal (1,0,0), area 36.8mm2, adj f0,f81,f331,f333
  f333: cylinder r=2.12mm len=4.24mm, axis (0,0,1), area 19.5mm2, adj f0,f81,f332,f334
  f334: plane 12.6x2.92mm, normal (-1,0,0), area 36.8mm2, adj f0,f81,f331,f333
  f335: cylinder r=2.12mm len=4.24mm, axis (0,0,1), area 19.5mm2, adj f0,f81,f336,f338
  f336: plane 12.6x2.92mm, normal (0,-1,0), area 36.8mm2, adj f0,f81,f335,f337
  f337: cylinder r=2.12mm len=4.24mm, axis (0,0,1), area 19.5mm2, adj f0,f81,f336,f338
  f338: plane 12.6x2.92mm, normal (0,1,0), area 36.8mm2, adj f0,f81,f335,f337
  f339: cylinder r=2.12mm len=4.24mm, axis (0,0,1), area 19.5mm2, adj f0,f81,f340,f342
  f340: plane 12.6x2.92mm, normal (-1,0,0), area 36.8mm2, adj f0,f81,f339,f341
  f341: cylinder r=2.12mm len=4.24mm, axis (0,0,1), area 19.5mm2, adj f0,f81,f340,f342
  f342: plane 12.6x2.92mm, normal (1,0,0), area 36.8mm2, adj f0,f81,f339,f341
  f343: cylinder r=2.13mm len=4.27mm, axis (0,0,1), area 39.2mm2, adj f0,f81
  f344: cylinder r=2.13mm len=4.27mm, axis (0,0,1), area 39.2mm2, adj f0,f81
  f345: cylinder r=2.13mm len=4.27mm, axis (0,0,1), area 39.2mm2, adj f0,f81
  f346: cylinder r=2.13mm len=4.27mm, axis (0,0,1), area 39.2mm2, adj f0,f81
  f347: cylinder r=2.13mm len=4.27mm, axis (0,0,1), area 39.2mm2, adj f0,f81
  f348: cylinder r=2.13mm len=4.27mm, axis (0,0,1), area 39.2mm2, adj f0,f81
  f349: cylinder r=2.13mm len=4.27mm, axis (0,0,1), area 39.2mm2, adj f0,f81
  f350: cylinder r=2.13mm len=4.27mm, axis (0,0,1), area 39.2mm2, adj f0,f81
PLACE A t=(-81.47,13.09,2.77)mm
PLACE B rot(axis=(1,0,0),90deg) t=(-81.47,60.63,2.77)mm
PLACE C rot(axis=(0,0,-1),89deg) t=(0,0,-1.46)mm
MATE revolute B.f1 <-> A.f0  axis (0,1,0) through (-81.47,28.84,2.77)mm
